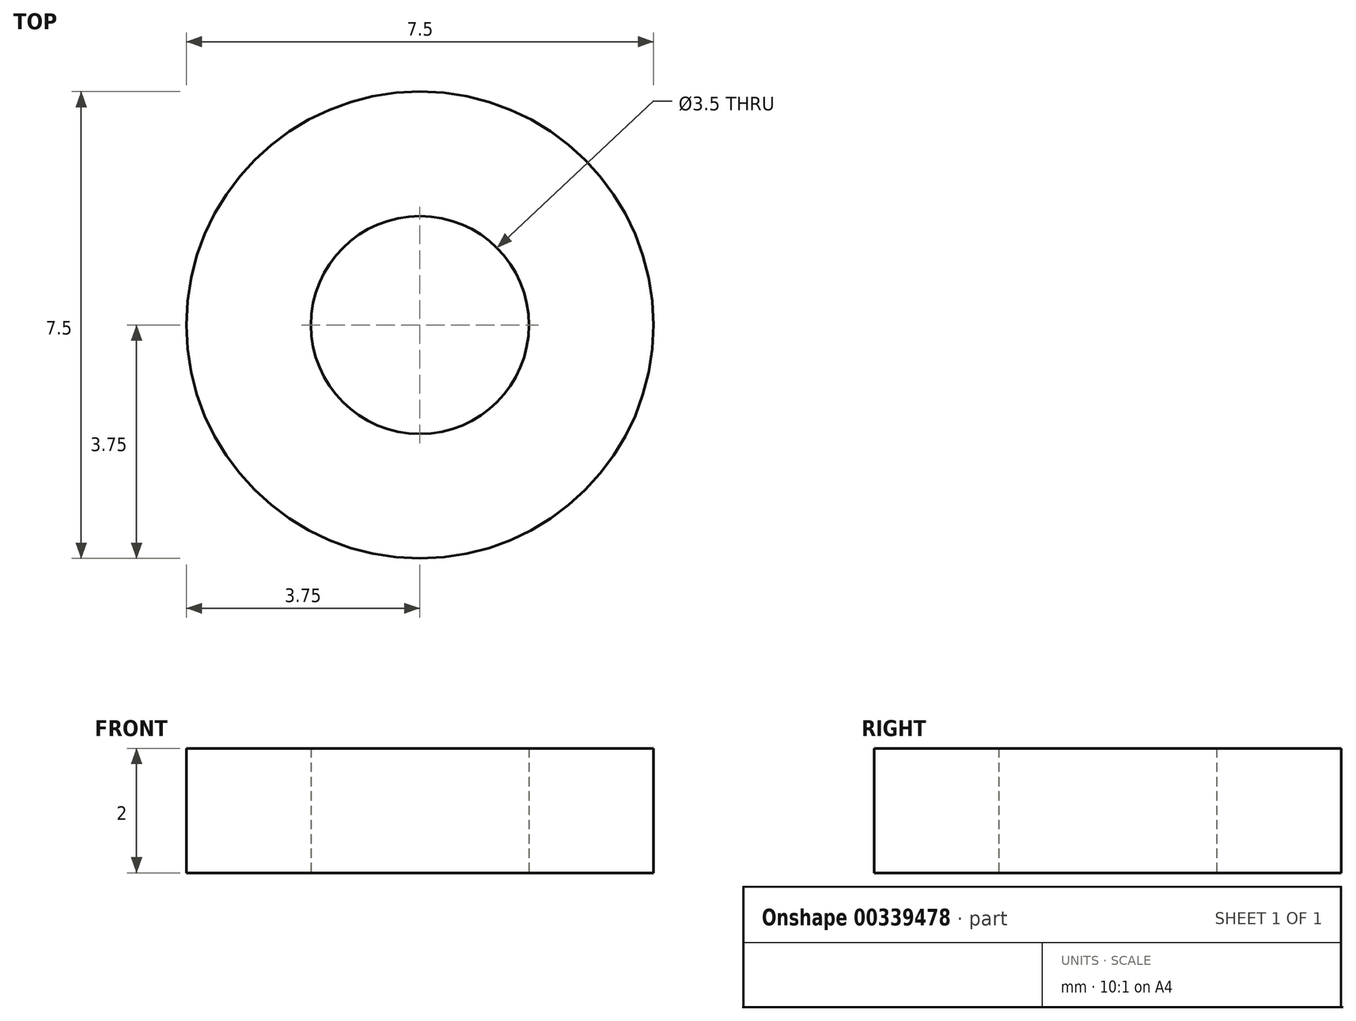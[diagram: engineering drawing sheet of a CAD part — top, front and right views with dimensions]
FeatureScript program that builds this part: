
annotation { "Feature Type Name" : "Feature", "Feature Type Description" : "" }
export const myFeature = defineFeature(function(context is Context, id is Id, definition is map)
    precondition{}
    {
        {
            var Q0;
            Q0=qCreatedBy(makeId("Top.planeOp"),FACE);
            var sketch = newSketch(context, id + "F0", { "sketchPlane" : qUnion([Q0])});
            skCircle(sketch, "E0", {"center": v(0, 0) * mm, "radius": 3.75 * mm});
            skCircle(sketch, "E1", {"center": v(0, 0) * mm, "radius": 1.75 * mm});
            skSolve(sketch);
        }
        {
            var Q0;
            Q0=makeQuery(id+"F0.imprint","IMPRINT",FACE,{"disambiguationData":[TD([[makeQuery(id+"F0.imprint","IMPRINT",EDGE,{"derivedFrom":sQuery(id+"F0.wireOp",EDGE,"E0")}),1.0]])]});
            extrude(context, id + "F1", {"entities" : qUnion([Q0]), "depth" : 2 * mm});
        }
    });
